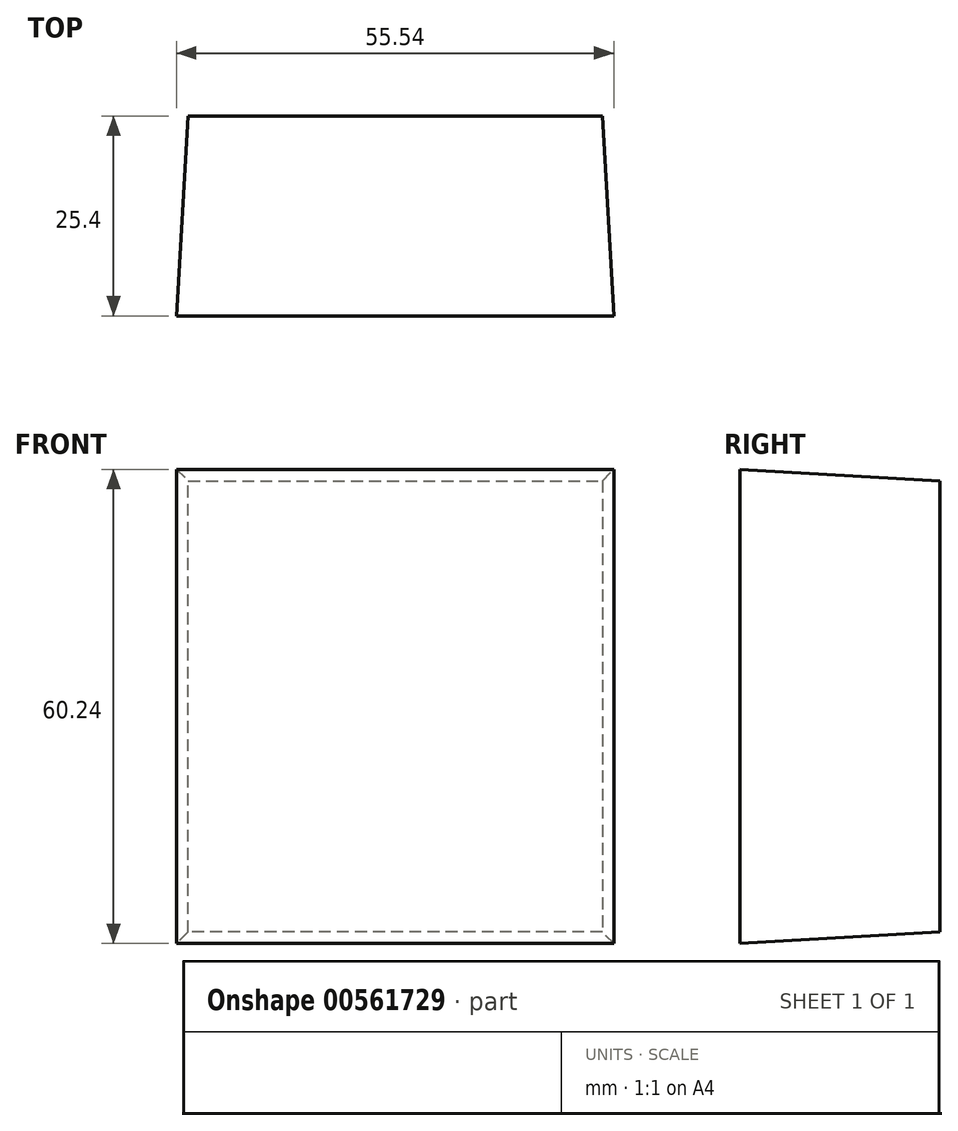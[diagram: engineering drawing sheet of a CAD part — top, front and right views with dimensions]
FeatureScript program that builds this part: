
annotation { "Feature Type Name" : "Feature", "Feature Type Description" : "" }
export const myFeature = defineFeature(function(context is Context, id is Id, definition is map)
    precondition{}
    {
        {
            var Q0;
            Q0=qCreatedBy(makeId("Front.planeOp"),FACE);
            var sketch = newSketch(context, id + "F0", { "sketchPlane" : qUnion([Q0])});
            skLineSegment(sketch, "E0.bottom", {"start": v(0, 0) * mm, "end": v(52.62, 0) * mm});
            skLineSegment(sketch, "E0.top", {"start": v(0, 57.31) * mm, "end": v(52.62, 57.31) * mm});
            skLineSegment(sketch, "E0.left", {"start": v(0, 0) * mm, "end": v(0, 57.31) * mm});
            skLineSegment(sketch, "E0.right", {"start": v(52.62, 0) * mm, "end": v(52.62, 57.31) * mm});
            skSolve(sketch);
        }
        {
            var Q0;
            Q0=makeQuery(id+"F0.imprint","IMPRINT",FACE,{"disambiguationData":[TD([[makeQuery(id+"F0.imprint","IMPRINT",EDGE,{"derivedFrom":sQuery(id+"F0.wireOp",EDGE,"E0.bottom")}),1.0]])]});
            extrude(context, id + "F1", {"entities" : qUnion([Q0]), "depth" : 25.4 * mm, "offsetDistance" : 25.4 * mm, "hasDraft" : true, "draftAngle" : 3.3 * degree});
        }
    });
